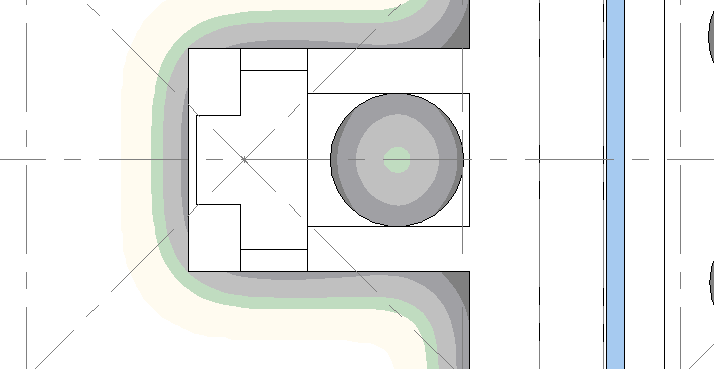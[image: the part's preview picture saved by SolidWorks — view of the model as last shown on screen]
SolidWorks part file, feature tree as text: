
SOLIDWORKS PART (.sldprt)
format: sldprt  version: not decoded by parser v0  size: 638,464 bytes
history: native  units: mm
features: sketch x13, cut_extrude x7, extrude x5 + 1 further entry (+10 scaffold rows collapsed)
feature tree (36):
  "Annotations"  RD1=39.025mm RD2=42mm RD3=42mm RD4=35mm
  scaffold x10  (default folders/planes/origin — collapsed)
  sketch  "Sketch4"  dims[c1.D20=~12.224278mm c1.D1=58.32mm c1.D2=31.0mm c1.D3=15.58mm c1.D4=31.0mm c1.D5=147.6375mm c1.D6=15.5mm c1.D7=15.5mm c1.D8=5.5mm c1.D9=5.5mm c1.D10=5.5mm c1.D11=5.5mm c1.D12=5.5mm c1.D13=5.5mm c1.D14=3.175mm c1.D15=3.175mm c1.D16=3.175mm c1.D17=3.175mm c1.D18=~73.931507mm c1.D19=3.175mm c2.D18=42.0mm c2.D20=42.0mm c3.D20=~178.954708deg]
  sketch  "Sketch5"  dims[D1=~4.829936mm]
  extrude  "Extrude1"  Depth=5mm
  sketch  "Sketch6"  dims[D1=~4.306344mm]
  extrude  "Extrude2"  Depth=35mm
  sketch  "Sketch7"
  extrude  "Extrude3"  Depth=13.175mm
  sketch  "Sketch9"
  cut_extrude  "Cut-Extrude2"  [1 undecoded]
  sketch  "Sketch13"
  cut_extrude  "Cut-Extrude4"  Depth=2mm
  sketch  "Sketch15"
  cut_extrude  "Cut-Extrude5"  Depth=5mm
  sketch  "Sketch16"
  cut_extrude  "Cut-Extrude6"  [1 undecoded]
  sketch  "Sketch10"
  cut_extrude  "Cut-Extrude7"  Depth=5mm
  sketch  "Sketch17"
  extrude  "Extrude9"  Depth=5mm
  sketch  "Sketch18"  dims[D1=~1.832738mm]
  cut_extrude  "Cut-Extrude8"  [1 undecoded]
  sketch  "Sketch20"  dims[D1=~2.963913mm]
  extrude  "Extrude11"  [1 undecoded]
  sketch  "Sketch21"
  cut_extrude  "Cut-Extrude9"  Depth=1mm
decode coverage: 13 of 25 modeling features carry decoded parameters; 1 rows unclassified (native names shown)
note: ~ marks probable driven/reference dimensions
note: 4 parameter values undecoded
summary: no parameter record found for 4 features
note: suppression state not decoded; provenance and decode notes live in map.json
